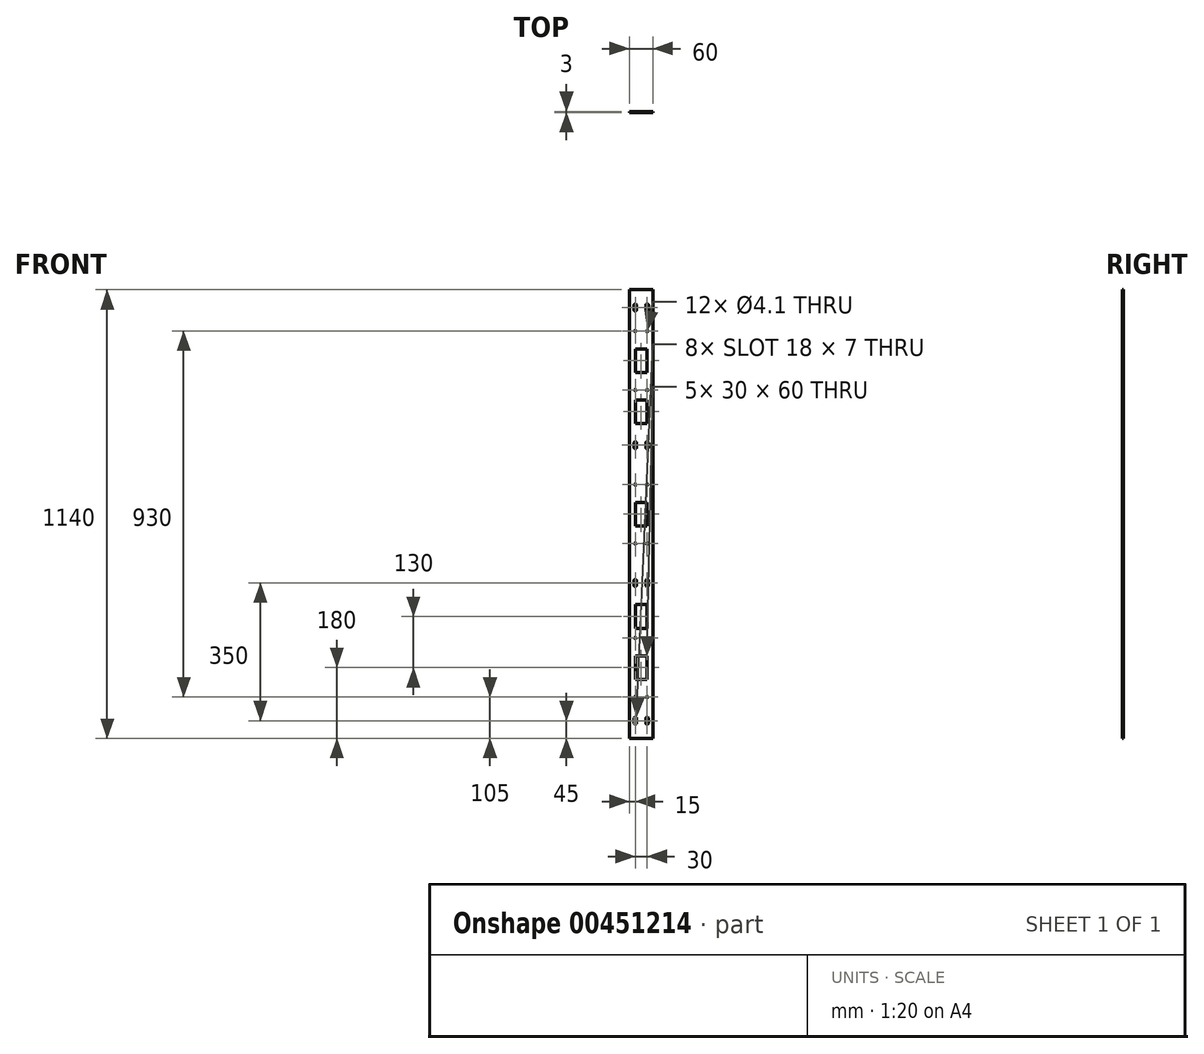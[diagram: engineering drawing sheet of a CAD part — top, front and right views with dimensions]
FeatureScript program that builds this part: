
annotation { "Feature Type Name" : "Feature", "Feature Type Description" : "" }
export const myFeature = defineFeature(function(context is Context, id is Id, definition is map)
    precondition{}
    {
        {
            var Q0;
            Q0=qCreatedBy(makeId("Front.planeOp"),FACE);
            var sketch = newSketch(context, id + "F0", { "sketchPlane" : qUnion([Q0])});
            skLineSegment(sketch, "E0.bottom", {"start": v(30, -570) * mm, "end": v(-30, -570) * mm});
            skLineSegment(sketch, "E0.top", {"start": v(30, 570) * mm, "end": v(-30, 570) * mm});
            skLineSegment(sketch, "E0.left", {"start": v(30, -570) * mm, "end": v(30, 570) * mm});
            skLineSegment(sketch, "E0.right", {"start": v(-30, -570) * mm, "end": v(-30, 570) * mm});
            skPoint(sketch, "E0.middle", {"position": v(0, 0) * mm});
            skLineSegment(sketch, "E1.bottom", {"start": v(-11.5, -530.5) * mm, "end": v(-18.5, -530.5) * mm, "construction": true});
            skLineSegment(sketch, "E1.top", {"start": v(-11.5, -519.5) * mm, "end": v(-18.5, -519.5) * mm, "construction": true});
            skLineSegment(sketch, "E1.left", {"start": v(-11.5, -530.5) * mm, "end": v(-11.5, -519.5) * mm});
            skLineSegment(sketch, "E1.right", {"start": v(-18.5, -530.5) * mm, "end": v(-18.5, -519.5) * mm});
            skPoint(sketch, "E1.middle", {"position": v(-15, -525) * mm});
            skArc(sketch, "E2", {"start": v(-11.5, -519.5) * mm, "mid": v(-15, -516) * mm, "end": v(-18.5, -519.5) * mm});
            skArc(sketch, "E3", {"start": v(-18.5, -530.5) * mm, "mid": v(-15, -534) * mm, "end": v(-11.5, -530.5) * mm});
            skLineSegment(sketch, "E4.bottom", {"start": v(18.5, -530.5) * mm, "end": v(11.5, -530.5) * mm, "construction": true});
            skLineSegment(sketch, "E4.top", {"start": v(18.5, -519.5) * mm, "end": v(11.5, -519.5) * mm, "construction": true});
            skLineSegment(sketch, "E4.left", {"start": v(18.5, -530.5) * mm, "end": v(18.5, -519.5) * mm});
            skLineSegment(sketch, "E4.right", {"start": v(11.5, -530.5) * mm, "end": v(11.5, -519.5) * mm});
            skPoint(sketch, "E4.middle", {"position": v(15, -525) * mm});
            skArc(sketch, "E5", {"start": v(18.5, -519.5) * mm, "mid": v(15, -516) * mm, "end": v(11.5, -519.5) * mm});
            skArc(sketch, "E6", {"start": v(11.5, -530.5) * mm, "mid": v(15, -534) * mm, "end": v(18.5, -530.5) * mm});
            skPoint(sketch, "E7.0.1.0", {"position": v(-15, -175) * mm});
            skArc(sketch, "E7.0.1.1", {"start": v(-11.5, -169.5) * mm, "mid": v(-15, -166) * mm, "end": v(-18.5, -169.5) * mm});
            skArc(sketch, "E7.0.1.2", {"start": v(-18.5, -180.5) * mm, "mid": v(-15, -184) * mm, "end": v(-11.5, -180.5) * mm});
            skPoint(sketch, "E7.0.1.3", {"position": v(15, -175) * mm});
            skArc(sketch, "E7.0.1.4", {"start": v(11.5, -180.5) * mm, "mid": v(15, -184) * mm, "end": v(18.5, -180.5) * mm});
            skLineSegment(sketch, "E7.0.1.5", {"start": v(11.5, -180.5) * mm, "end": v(11.5, -169.5) * mm});
            skLineSegment(sketch, "E7.0.1.6", {"start": v(18.5, -180.5) * mm, "end": v(18.5, -169.5) * mm});
            skLineSegment(sketch, "E7.0.1.7", {"start": v(-11.5, -180.5) * mm, "end": v(-18.5, -180.5) * mm, "construction": true});
            skLineSegment(sketch, "E7.0.1.8", {"start": v(-18.5, -180.5) * mm, "end": v(-18.5, -169.5) * mm});
            skArc(sketch, "E7.0.1.9", {"start": v(18.5, -169.5) * mm, "mid": v(15, -166) * mm, "end": v(11.5, -169.5) * mm});
            skLineSegment(sketch, "E7.0.1.10", {"start": v(-11.5, -169.5) * mm, "end": v(-18.5, -169.5) * mm, "construction": true});
            skLineSegment(sketch, "E7.0.1.11", {"start": v(-11.5, -180.5) * mm, "end": v(-11.5, -169.5) * mm});
            skLineSegment(sketch, "E7.0.1.12", {"start": v(18.5, -180.5) * mm, "end": v(11.5, -180.5) * mm, "construction": true});
            skLineSegment(sketch, "E7.0.1.13", {"start": v(18.5, -169.5) * mm, "end": v(11.5, -169.5) * mm, "construction": true});
            skPoint(sketch, "E7.0.2.0", {"position": v(-15, 175) * mm});
            skArc(sketch, "E7.0.2.1", {"start": v(-11.5, 180.5) * mm, "mid": v(-15, 184) * mm, "end": v(-18.5, 180.5) * mm});
            skArc(sketch, "E7.0.2.2", {"start": v(-18.5, 169.5) * mm, "mid": v(-15, 166) * mm, "end": v(-11.5, 169.5) * mm});
            skPoint(sketch, "E7.0.2.3", {"position": v(15, 175) * mm});
            skArc(sketch, "E7.0.2.4", {"start": v(11.5, 169.5) * mm, "mid": v(15, 166) * mm, "end": v(18.5, 169.5) * mm});
            skLineSegment(sketch, "E7.0.2.5", {"start": v(11.5, 169.5) * mm, "end": v(11.5, 180.5) * mm});
            skLineSegment(sketch, "E7.0.2.6", {"start": v(18.5, 169.5) * mm, "end": v(18.5, 180.5) * mm});
            skLineSegment(sketch, "E7.0.2.7", {"start": v(-11.5, 169.5) * mm, "end": v(-18.5, 169.5) * mm, "construction": true});
            skLineSegment(sketch, "E7.0.2.8", {"start": v(-18.5, 169.5) * mm, "end": v(-18.5, 180.5) * mm});
            skArc(sketch, "E7.0.2.9", {"start": v(18.5, 180.5) * mm, "mid": v(15, 184) * mm, "end": v(11.5, 180.5) * mm});
            skLineSegment(sketch, "E7.0.2.10", {"start": v(-11.5, 180.5) * mm, "end": v(-18.5, 180.5) * mm, "construction": true});
            skLineSegment(sketch, "E7.0.2.11", {"start": v(-11.5, 169.5) * mm, "end": v(-11.5, 180.5) * mm});
            skLineSegment(sketch, "E7.0.2.12", {"start": v(18.5, 169.5) * mm, "end": v(11.5, 169.5) * mm, "construction": true});
            skLineSegment(sketch, "E7.0.2.13", {"start": v(18.5, 180.5) * mm, "end": v(11.5, 180.5) * mm, "construction": true});
            skLineSegment(sketch, "E7.direction1", {"start": v(-18.5, -530.5) * mm, "end": v(6.5, -530.5) * mm, "construction": true});
            skLineSegment(sketch, "E7.direction2", {"start": v(-18.5, -530.5) * mm, "end": v(-18.5, -180.5) * mm, "construction": true});
            skPoint(sketch, "E8.0.0.3", {"position": v(-15, 525) * mm});
            skArc(sketch, "E8.1.0.3", {"start": v(-11.5, 530.5) * mm, "mid": v(-15, 534) * mm, "end": v(-18.5, 530.5) * mm});
            skArc(sketch, "E8.5.0.3", {"start": v(-18.5, 519.5) * mm, "mid": v(-15, 516) * mm, "end": v(-11.5, 519.5) * mm});
            skPoint(sketch, "E8.9.0.3", {"position": v(15, 525) * mm});
            skArc(sketch, "E8.10.0.3", {"start": v(11.5, 519.5) * mm, "mid": v(15, 516) * mm, "end": v(18.5, 519.5) * mm});
            skLineSegment(sketch, "E8.14.0.3", {"start": v(11.5, 519.5) * mm, "end": v(11.5, 530.5) * mm});
            skLineSegment(sketch, "E8.17.0.3", {"start": v(18.5, 519.5) * mm, "end": v(18.5, 530.5) * mm});
            skLineSegment(sketch, "E8.20.0.3", {"start": v(-11.5, 519.5) * mm, "end": v(-18.5, 519.5) * mm, "construction": true});
            skLineSegment(sketch, "E8.23.0.3", {"start": v(-18.5, 519.5) * mm, "end": v(-18.5, 530.5) * mm});
            skArc(sketch, "E8.26.0.3", {"start": v(18.5, 530.5) * mm, "mid": v(15, 534) * mm, "end": v(11.5, 530.5) * mm});
            skLineSegment(sketch, "E8.30.0.3", {"start": v(-11.5, 530.5) * mm, "end": v(-18.5, 530.5) * mm, "construction": true});
            skLineSegment(sketch, "E8.33.0.3", {"start": v(-11.5, 519.5) * mm, "end": v(-11.5, 530.5) * mm});
            skLineSegment(sketch, "E8.36.0.3", {"start": v(18.5, 519.5) * mm, "end": v(11.5, 519.5) * mm, "construction": true});
            skLineSegment(sketch, "E8.39.0.3", {"start": v(18.5, 530.5) * mm, "end": v(11.5, 530.5) * mm, "construction": true});
            skSolve(sketch);
        }
        {
            var Q0;
            Q0 = qSketchRegion(id + "F0", true);
            extrude(context, id + "F1", {"entities" : qUnion([Q0]), "depth" : 3 * mm, "offsetDistance" : 25 * mm});
        }
        {
            var Q0;
            Q0=makeQuery(id+"F1.opExtrude","CAP_FACE",FACE,{"disambiguationData":[OSD([sQuery(id+"F0.wireOp",EDGE,"E0.bottom"),sQuery(id+"F0.wireOp",EDGE,"E0.top"),sQuery(id+"F0.wireOp",EDGE,"E0.left"),sQuery(id+"F0.wireOp",EDGE,"E0.right"),sQuery(id+"F0.wireOp",EDGE,"E1.left"),sQuery(id+"F0.wireOp",EDGE,"E1.right"),sQuery(id+"F0.wireOp",EDGE,"E2"),sQuery(id+"F0.wireOp",EDGE,"E3"),sQuery(id+"F0.wireOp",EDGE,"E4.left"),sQuery(id+"F0.wireOp",EDGE,"E4.right"),sQuery(id+"F0.wireOp",EDGE,"E5"),sQuery(id+"F0.wireOp",EDGE,"E6"),sQuery(id+"F0.wireOp",EDGE,"E7.0.1.1"),sQuery(id+"F0.wireOp",EDGE,"E7.0.1.2"),sQuery(id+"F0.wireOp",EDGE,"E7.0.1.4"),sQuery(id+"F0.wireOp",EDGE,"E7.0.1.5"),sQuery(id+"F0.wireOp",EDGE,"E7.0.1.6"),sQuery(id+"F0.wireOp",EDGE,"E7.0.1.8"),sQuery(id+"F0.wireOp",EDGE,"E7.0.1.9"),sQuery(id+"F0.wireOp",EDGE,"E7.0.1.11"),sQuery(id+"F0.wireOp",EDGE,"E7.0.2.1"),sQuery(id+"F0.wireOp",EDGE,"E7.0.2.2"),sQuery(id+"F0.wireOp",EDGE,"E7.0.2.4"),sQuery(id+"F0.wireOp",EDGE,"E7.0.2.5"),sQuery(id+"F0.wireOp",EDGE,"E7.0.2.6"),sQuery(id+"F0.wireOp",EDGE,"E7.0.2.8"),sQuery(id+"F0.wireOp",EDGE,"E7.0.2.9"),sQuery(id+"F0.wireOp",EDGE,"E7.0.2.11")])],"isStart":false});
            var sketch = newSketch(context, id + "F2", { "sketchPlane" : qUnion([Q0])});
            skCircle(sketch, "E9", {"center": v(-15, -465) * mm, "radius": 2.05 * mm});
            skCircle(sketch, "E10", {"center": v(15, -465) * mm, "radius": 2.05 * mm});
            skCircle(sketch, "E11", {"center": v(-15, -315) * mm, "radius": 2.05 * mm});
            skCircle(sketch, "E12", {"center": v(15, -315) * mm, "radius": 2.05 * mm});
            skLineSegment(sketch, "E13", {"start": v(-192.33, 210) * mm, "end": v(278.17, 210) * mm, "construction": true});
            skLineSegment(sketch, "E14", {"start": v(-196.55, -210) * mm, "end": v(305.6, -210) * mm, "construction": true});
            skCircle(sketch, "E15", {"center": v(-15, -75) * mm, "radius": 2.05 * mm});
            skCircle(sketch, "E16", {"center": v(15, -75) * mm, "radius": 2.05 * mm});
            skCircle(sketch, "E17", {"center": v(-15, 75) * mm, "radius": 2.05 * mm});
            skCircle(sketch, "E18", {"center": v(15, 75) * mm, "radius": 2.05 * mm});
            skCircle(sketch, "E19", {"center": v(-15, 315) * mm, "radius": 2.05 * mm});
            skCircle(sketch, "E20", {"center": v(15, 315) * mm, "radius": 2.05 * mm});
            skCircle(sketch, "E21", {"center": v(-15, 465) * mm, "radius": 2.05 * mm});
            skCircle(sketch, "E22", {"center": v(15, 465) * mm, "radius": 2.05 * mm});
            skLineSegment(sketch, "E23.bottom", {"start": v(15, -420) * mm, "end": v(-15, -420) * mm});
            skLineSegment(sketch, "E23.top", {"start": v(15, -360) * mm, "end": v(-15, -360) * mm});
            skLineSegment(sketch, "E23.left", {"start": v(15, -420) * mm, "end": v(15, -360) * mm});
            skLineSegment(sketch, "E23.right", {"start": v(-15, -420) * mm, "end": v(-15, -360) * mm});
            skPoint(sketch, "E23.middle", {"position": v(0, -390) * mm});
            skLineSegment(sketch, "E24.bottom", {"start": v(15, -290) * mm, "end": v(-15, -290) * mm});
            skLineSegment(sketch, "E24.top", {"start": v(15, -230) * mm, "end": v(-15, -230) * mm});
            skLineSegment(sketch, "E24.left", {"start": v(15, -290) * mm, "end": v(15, -230) * mm});
            skLineSegment(sketch, "E24.right", {"start": v(-15, -290) * mm, "end": v(-15, -230) * mm});
            skPoint(sketch, "E24.middle", {"position": v(0, -260) * mm});
            skLineSegment(sketch, "E25.bottom", {"start": v(15, 360) * mm, "end": v(-15, 360) * mm});
            skLineSegment(sketch, "E25.top", {"start": v(15, 420) * mm, "end": v(-15, 420) * mm});
            skLineSegment(sketch, "E25.left", {"start": v(15, 360) * mm, "end": v(15, 420) * mm});
            skLineSegment(sketch, "E25.right", {"start": v(-15, 360) * mm, "end": v(-15, 420) * mm});
            skPoint(sketch, "E25.middle", {"position": v(0, 390) * mm});
            skLineSegment(sketch, "E26.bottom", {"start": v(15, 230) * mm, "end": v(-15, 230) * mm});
            skLineSegment(sketch, "E26.top", {"start": v(15, 290) * mm, "end": v(-15, 290) * mm});
            skLineSegment(sketch, "E26.left", {"start": v(15, 230) * mm, "end": v(15, 290) * mm});
            skLineSegment(sketch, "E26.right", {"start": v(-15, 230) * mm, "end": v(-15, 290) * mm});
            skPoint(sketch, "E26.middle", {"position": v(0, 260) * mm});
            skLineSegment(sketch, "E27.bottom", {"start": v(15, -30) * mm, "end": v(-15, -30) * mm});
            skLineSegment(sketch, "E27.top", {"start": v(15, 30) * mm, "end": v(-15, 30) * mm});
            skLineSegment(sketch, "E27.left", {"start": v(15, -30) * mm, "end": v(15, 30) * mm});
            skLineSegment(sketch, "E27.right", {"start": v(-15, -30) * mm, "end": v(-15, 30) * mm});
            skPoint(sketch, "E27.middle", {"position": v(0, 0) * mm});
            skSolve(sketch);
        }
        {
            var Q0;
            Q0 = qSketchRegion(id + "F2", true);
            extrude(context, id + "F3", {"entities" : qUnion([Q0]), "operationType" : NewBodyOperationType.REMOVE, "oppositeDirection" : true, "depth" : 25 * mm, "offsetDistance" : 25 * mm});
        }
    });
